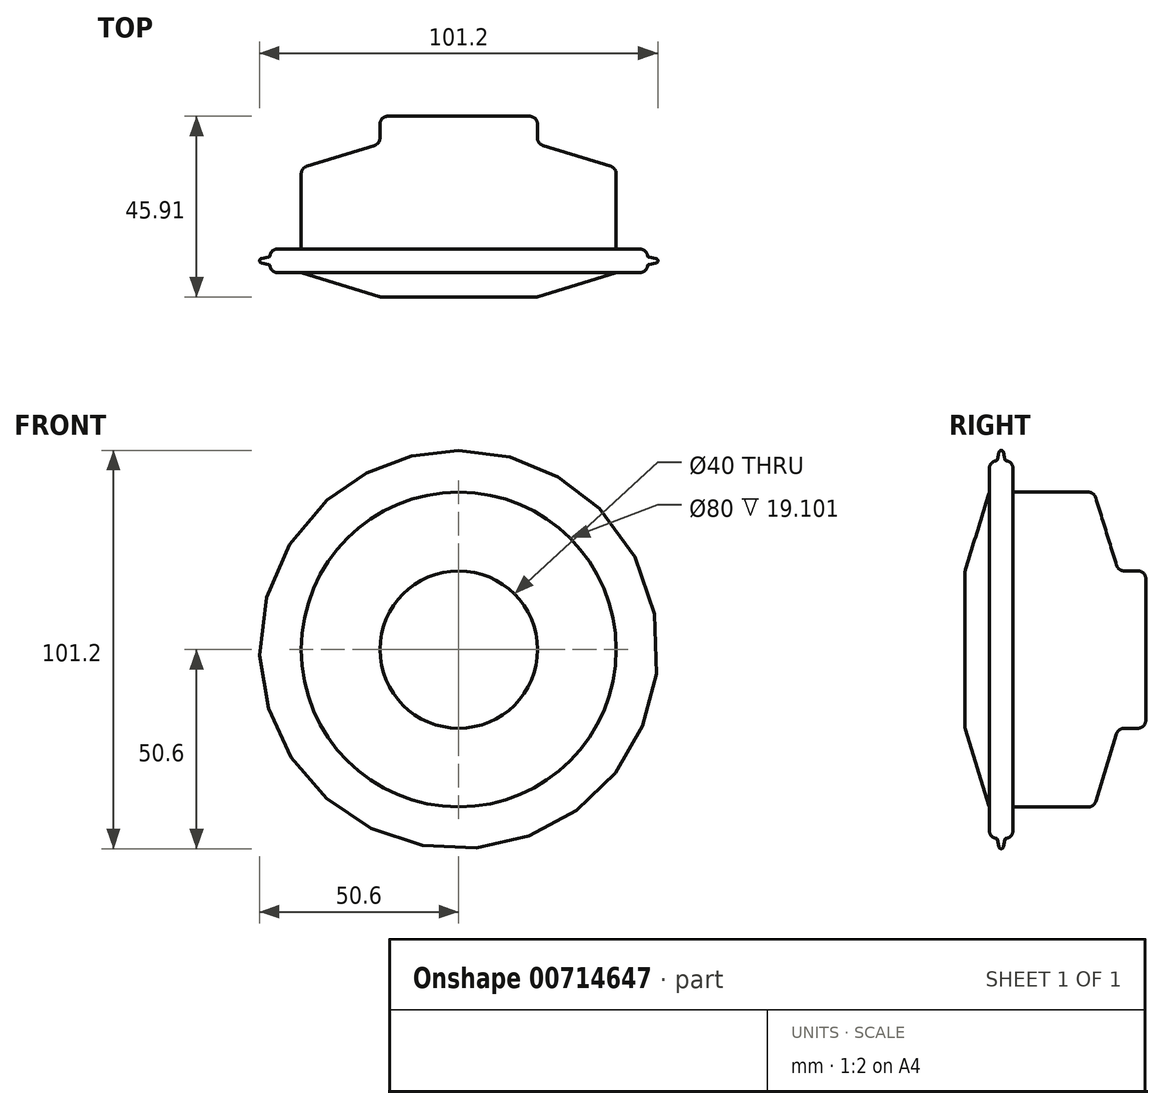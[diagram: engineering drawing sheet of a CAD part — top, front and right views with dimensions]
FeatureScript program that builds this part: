
annotation { "Feature Type Name" : "Feature", "Feature Type Description" : "" }
export const myFeature = defineFeature(function(context is Context, id is Id, definition is map)
    precondition{}
    {
        {
            var Q0;
            Q0=qCreatedBy(makeId("Top.planeOp"),FACE);
            var sketch = newSketch(context, id + "F0", { "sketchPlane" : qUnion([Q0])});
            skLineSegment(sketch, "E0", {"start": v(20.29, 0.09) * mm, "end": v(39.71, 6.09) * mm});
            skLineSegment(sketch, "E1", {"start": v(40, 12.17) * mm, "end": v(40, 31.28) * mm});
            skLineSegment(sketch, "E2", {"start": v(38.59, 33.19) * mm, "end": v(21.41, 38.5) * mm});
            skLineSegment(sketch, "E3", {"start": v(20, 40.4) * mm, "end": v(20, 43.9) * mm});
            skLineSegment(sketch, "E4", {"start": v(18, 45.9) * mm, "end": v(0, 45.9) * mm});
            skLineSegment(sketch, "E5", {"start": v(40.3, 6.17) * mm, "end": v(46, 6.17) * mm});
            skLineSegment(sketch, "E6", {"start": v(46, 12.17) * mm, "end": v(40, 12.17) * mm});
            skArc(sketch, "E7.filletArc", {"start": v(47.98, 10.43) * mm, "mid": v(47.32, 11.68) * mm, "end": v(46, 12.17) * mm});
            skArc(sketch, "E8.filletArc", {"start": v(46, 6.17) * mm, "mid": v(47.32, 6.67) * mm, "end": v(47.98, 7.91) * mm});
            skArc(sketch, "E9.filletArc", {"start": v(20, 43.9) * mm, "mid": v(19.41, 45.32) * mm, "end": v(18, 45.9) * mm});
            skArc(sketch, "E10.filletArc", {"start": v(20, 40.4) * mm, "mid": v(20.4, 39.21) * mm, "end": v(21.41, 38.5) * mm});
            skArc(sketch, "E11.filletArc", {"start": v(40, 31.28) * mm, "mid": v(39.6, 32.46) * mm, "end": v(38.59, 33.19) * mm});
            skArc(sketch, "E12.filletArc", {"start": v(40.3, 6.17) * mm, "mid": v(40, 6.15) * mm, "end": v(39.71, 6.09) * mm});
            skArc(sketch, "E13.filletArc", {"start": v(19.7, 0) * mm, "mid": v(20, 0.02) * mm, "end": v(20.29, 0.09) * mm});
            skLineSegment(sketch, "E14", {"start": v(48.28, 10.12) * mm, "end": v(50.11, 9.76) * mm});
            skLineSegment(sketch, "E15", {"start": v(50.11, 8.59) * mm, "end": v(48.28, 8.23) * mm});
            skArc(sketch, "E16.filletArc", {"start": v(50.11, 8.59) * mm, "mid": v(50.6, 9.17) * mm, "end": v(50.11, 9.76) * mm});
            skArc(sketch, "E17.filletArc", {"start": v(47.98, 10.43) * mm, "mid": v(48.08, 10.23) * mm, "end": v(48.28, 10.12) * mm});
            skArc(sketch, "E18.filletArc", {"start": v(48.28, 8.23) * mm, "mid": v(48.08, 8.12) * mm, "end": v(47.98, 7.91) * mm});
            skLineSegment(sketch, "E19", {"start": v(19.7, 0) * mm, "end": v(0, 0) * mm});
            skLineSegment(sketch, "E20", {"start": v(0, -7.11) * mm, "end": v(0, 69) * mm, "construction": true});
            skSolve(sketch);
        }
        {
            var Q0;
            Q0=sQuery(id+"F0.wireOp",EDGE,"E4");
            var Q1;
            Q1=sQuery(id+"F0.wireOp",EDGE,"E1");
            var Q2;
            Q2=sQuery(id+"F0.wireOp",EDGE,"E0");
            var Q3;
            Q3=sQuery(id+"F0.wireOp",EDGE,"E2");
            var Q4;
            Q4=sQuery(id+"F0.wireOp",EDGE,"E19");
            var Q5;
            Q5=sQuery(id+"F0.wireOp",EDGE,"E5");
            var Q6;
            Q6=sQuery(id+"F0.wireOp",EDGE,"E6");
            var Q7;
            Q7=sQuery(id+"F0.wireOp",EDGE,"E13.filletArc");
            var Q8;
            Q8=sQuery(id+"F0.wireOp",EDGE,"E3");
            var Q9;
            Q9=sQuery(id+"F0.wireOp",EDGE,"E9.filletArc");
            var Q10;
            Q10=sQuery(id+"F0.wireOp",EDGE,"E10.filletArc");
            var Q11;
            Q11=sQuery(id+"F0.wireOp",EDGE,"E11.filletArc");
            var Q12;
            Q12=sQuery(id+"F0.wireOp",EDGE,"E12.filletArc");
            var Q13;
            Q13=sQuery(id+"F0.wireOp",EDGE,"E7.filletArc");
            var Q14;
            Q14=sQuery(id+"F0.wireOp",EDGE,"E8.filletArc");
            var Q15;
            Q15=sQuery(id+"F0.wireOp",EDGE,"E16.filletArc");
            var Q16;
            Q16=sQuery(id+"F0.wireOp",EDGE,"E17.filletArc");
            var Q17;
            Q17=sQuery(id+"F0.wireOp",EDGE,"E15");
            var Q18;
            Q18=sQuery(id+"F0.wireOp",EDGE,"E14");
            var Q19;
            Q19=sQuery(id+"F0.wireOp",EDGE,"E18.filletArc");
            var Q20;
            Q20=sQuery(id+"F0.wireOp",EDGE,"E20");
            revolve(context, id + "F1", {"bodyType" : ToolBodyType.SURFACE, "surfaceOperationType" : NewSurfaceOperationType.NEW, "surfaceEntities" : qUnion([Q0, Q1, Q2, Q3, Q4, Q5, Q6, Q7, Q8, Q9, Q10, Q11, Q12, Q13, Q14, Q15, Q16, Q17, Q18, Q19]), "axis" : qUnion([Q20]), "revolveType" : RevolveType.FULL});
        }
    });
